# Revit family: S-578 (EN)
name_source: partatom
category: Pipe Fittings
revit_build: Autodesk Revit 2015 (Build: 20140606_1530(x64)
units: mm (PartAtom-declared; Revit-internal decimal feet)

## types (6) — shared parameters
Appliances = SHOWERS Ø90
D = 40 mm  [stored 0.131234 ft]
DM = 42 mm  [stored 0.137795 ft]
Flowrate = 0.6 L/s
Inlets = Ø115 mm
Manufacturer = Jimten
Material = PP (White)
Model = S-578
ThicknessSWMax = 27 mm  [stored 0.0885827 ft]
TicknessSWMin = 2 mm  [stored 0.00656168 ft]
URL = http://www.jimten.com

## per-type parameters (varying)
| type | Description | Material cover | Outlet | Pipe 40/50 | Reference | Type Comments |
| S-578_40_STEEL INOX/CHROMED | JUNTAFIX SHOWER WASTE OUTLET TRAP, HORIZONTAL OUTLET, REDUCED HEIGHT, COVER IN CHROMED STAINLESS STEEL | Steel Inox/Chromed | Ø40 MM (FEMALE) | No | 012519 | 58 MM IN HEIGHT, EASY INSTALLATION THANKS TO ITS INTEGRATED JOINT SYSTEMS, WITH METAL FLANGE SYSTEM  FOR SHOWER TRAYS UP TO 26 MM IN THICKNESS WITH 3 SCREWS, INCLUDES ADAPTER TO PVC PIPES |
| S-578_40_STEEL INOX/SATIN | JUNTAFIX SHOWER WASTE OUTLET TRAP, HORIZONTAL OUTLET, REDUCED HEIGHT, COVER IN SATIN STAINLESS STEEL | Steel Inox/Satin | Ø40 MM (FEMALE) | No | 012279 | 58 MM IN HEIGHT, EASY INSTALLATION THANKS TO ITS INTEGRATED JOINT SYSTEMS, WITH METAL FLANGE SYSTEM  FOR SHOWER TRAYS UP TO 26 MM IN THICKNESS WITH 3 SCREWS, INCLUDES ADAPTER TO PVC PIPES |
| S-578_40/50_STEEL INOX/SATIN | JUNTAFIX SHOWER WASTE OUTLET TRAP, HORIZONTAL OUTLET, REDUCED HEIGHT, COVER IN SATIN STAINLESS STEEL | Steel Inox/Satin | Ø40/50 MM (MALE) | Yes | 012299 | 58 MM IN HEIGHT, EASY INSTALLATION THANKS TO ITS INTEGRATED JOINT SYSTEMS, WITH METAL FLANGE SYSTEM  FOR SHOWER TRAYS UP TO 26 MM IN THICKNESS WITH 3 SCREWS, INCLUDES ADAPTER TO 40/50 PIPES |
| S-578_40/50_STEEL INOX/CHROMED | JUNTAFIX SHOWER WASTE OUTLET TRAP, HORIZONTAL OUTLET, REDUCED HEIGHT, COVER IN CHROMED STAINLESS STEEL | Steel Inox/Chromed | Ø40/50 MM (MALE) | Yes | 012529 | 58 MM IN HEIGHT, EASY INSTALLATION THANKS TO ITS INTEGRATED JOINT SYSTEMS, WITH METAL FLANGE SYSTEM  FOR SHOWER TRAYS UP TO 26 MM IN THICKNESS WITH 3 SCREWS, INCLUDES ADAPTER TO 40/50 PIPES |
| S-578_40/50_WHITE | JUNTAFIX SHOWER WASTE OUTLET TRAP, HORIZONTAL OUTLET, REDUCED HEIGHT, WHITE COVER | ABS (White) | Ø40/50 MM (MALE) | Yes | 012929 | 58 MM IN HEIGHT, EASY INSTALLATION THANKS TO ITS INTEGRATED JOINT SYSTEMS, WITH METAL FLANGE SYSTEM  FOR SHOWER TRAYS UP TO 26 MM IN THICKNESS WITH 3 SCREWS, INCLUDES ADAPTER TO 40/50 PIPES |
| S-578_40_WHITE | JUNTAFIX SHOWER WASTE OUTLET TRAP, HORIZONTAL OUTLET, REDUCED HEIGHT, WHITE COVER | ABS (White) | Ø40 MM (FEMALE) | No | 012869 | 58 MM IN HEIGHT, EASY INSTALLATION THANKS TO ITS INTEGRATED JOINT SYSTEMS, WITH METAL FLANGE SYSTEM  FOR SHOWER TRAYS UP TO 26 MM IN THICKNESS WITH 3 SCREWS, INCLUDES ADAPTER TO PVC PIPES |

note: [stored X ft] marks values corroborated as IEEE doubles in the binary element streams (Revit-internal decimal feet)

## geometry (parser evidence)
native form markers: Blend x2
no freeform markers — native parametric forms only
